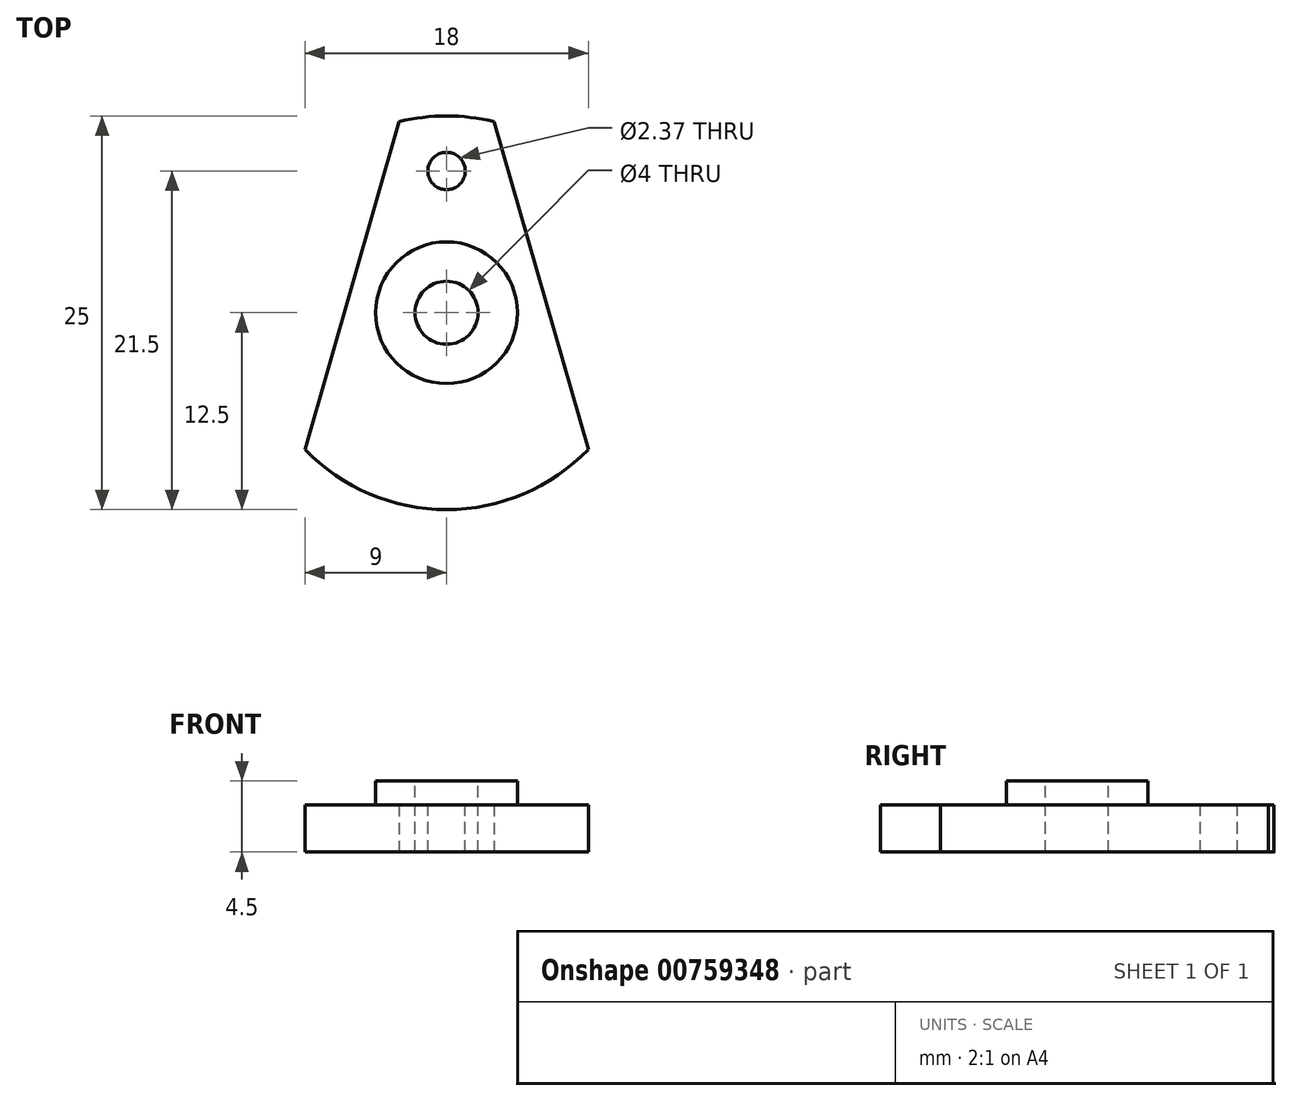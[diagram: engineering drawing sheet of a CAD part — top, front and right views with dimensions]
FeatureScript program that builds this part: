
annotation { "Feature Type Name" : "Feature", "Feature Type Description" : "" }
export const myFeature = defineFeature(function(context is Context, id is Id, definition is map)
    precondition{}
    {
        {
            var Q0;
            Q0=qCreatedBy(makeId("Top.planeOp"),FACE);
            var sketch = newSketch(context, id + "F0", { "sketchPlane" : qUnion([Q0])});
            skArc(sketch, "E0", {"start": v(-9, -8.67) * mm, "mid": v(0, -12.5) * mm, "end": v(9, -8.67) * mm});
            skLineSegment(sketch, "E1", {"start": v(3, 19.66) * mm, "end": v(3, -14.86) * mm, "construction": true});
            skLineSegment(sketch, "E2", {"start": v(9, 19.9) * mm, "end": v(9, -14.86) * mm, "construction": true});
            skLineSegment(sketch, "E3", {"start": v(3, 12.13) * mm, "end": v(9, -8.67) * mm});
            skLineSegment(sketch, "E4.MirrorCS", {"start": v(-3, 12.13) * mm, "end": v(-9, -8.67) * mm});
            skArc(sketch, "E5.trimOffspring", {"start": v(3, 12.13) * mm, "mid": v(0, 12.5) * mm, "end": v(-3, 12.13) * mm});
            skSolve(sketch);
        }
        {
            var Q0;
            Q0=makeQuery(id+"F0.imprint","IMPRINT",FACE,{"disambiguationData":[TD([[makeQuery(id+"F0.imprint","IMPRINT",EDGE,{"derivedFrom":sQuery(id+"F0.wireOp",EDGE,"E0")}),1.0]])]});
            extrude(context, id + "F1", {"entities" : qUnion([Q0]), "depth" : 3 * mm, "offsetDistance" : 25 * mm});
        }
        {
            var Q0;
            Q0=makeQuery(id+"F1.opExtrude","CAP_FACE",FACE,{"disambiguationData":[OSD([sQuery(id+"F0.wireOp",EDGE,"E0"),sQuery(id+"F0.wireOp",EDGE,"E3"),sQuery(id+"F0.wireOp",EDGE,"E4.MirrorCS"),sQuery(id+"F0.wireOp",EDGE,"E5.trimOffspring")])],"isStart":false});
            var sketch = newSketch(context, id + "F2", { "sketchPlane" : qUnion([Q0])});
            skCircle(sketch, "E6", {"center": v(0, 9) * mm, "radius": 1.19 * mm});
            skSolve(sketch);
        }
        {
            var Q0;
            Q0=makeQuery(id+"F2.imprint","IMPRINT",FACE,{"disambiguationData":[TD([[makeQuery(id+"F2.imprint","IMPRINT",EDGE,{"derivedFrom":sQuery(id+"F2.wireOp",EDGE,"E6")}),1.0]])]});
            extrude(context, id + "F3", {"entities" : qUnion([Q0]), "operationType" : NewBodyOperationType.REMOVE, "endBound" : BoundingType.THROUGH_ALL, "oppositeDirection" : true, "depth" : 25 * mm, "offsetDistance" : 25 * mm});
        }
        {
            var Q0;
            Q0=makeQuery(id+"F1.opExtrude","CAP_FACE",FACE,{"disambiguationData":[OSD([sQuery(id+"F0.wireOp",EDGE,"E0"),sQuery(id+"F0.wireOp",EDGE,"E3"),sQuery(id+"F0.wireOp",EDGE,"E4.MirrorCS"),sQuery(id+"F0.wireOp",EDGE,"E5.trimOffspring")])],"isStart":false});
            var sketch = newSketch(context, id + "F4", { "sketchPlane" : qUnion([Q0])});
            skCircle(sketch, "E7", {"center": v(0, 0) * mm, "radius": 4.5 * mm});
            skSolve(sketch);
        }
        {
            var Q0;
            Q0=makeQuery(id+"F4.imprint","IMPRINT",FACE,{"disambiguationData":[TD([[makeQuery(id+"F4.imprint","IMPRINT",EDGE,{"derivedFrom":sQuery(id+"F4.wireOp",EDGE,"E7")}),1.0]])]});
            extrude(context, id + "F5", {"entities" : qUnion([Q0]), "operationType" : NewBodyOperationType.ADD, "depth" : 1.5 * mm, "offsetDistance" : 25 * mm});
        }
        {
            var Q0;
            Q0=makeQuery(id+"F5.opExtrude","CAP_FACE",FACE,{"disambiguationData":[OSD([sQuery(id+"F4.wireOp",EDGE,"E7")])],"isStart":false});
            var sketch = newSketch(context, id + "F6", { "sketchPlane" : qUnion([Q0])});
            skCircle(sketch, "E8", {"center": v(0, 0) * mm, "radius": 2 * mm});
            skSolve(sketch);
        }
        {
            var Q0;
            Q0=makeQuery(id+"F6.imprint","IMPRINT",FACE,{"disambiguationData":[TD([[makeQuery(id+"F6.imprint","IMPRINT",EDGE,{"derivedFrom":sQuery(id+"F6.wireOp",EDGE,"E8")}),1.0]])]});
            extrude(context, id + "F7", {"entities" : qUnion([Q0]), "operationType" : NewBodyOperationType.REMOVE, "endBound" : BoundingType.THROUGH_ALL, "oppositeDirection" : true, "depth" : 25 * mm, "offsetDistance" : 25 * mm});
        }
    });
